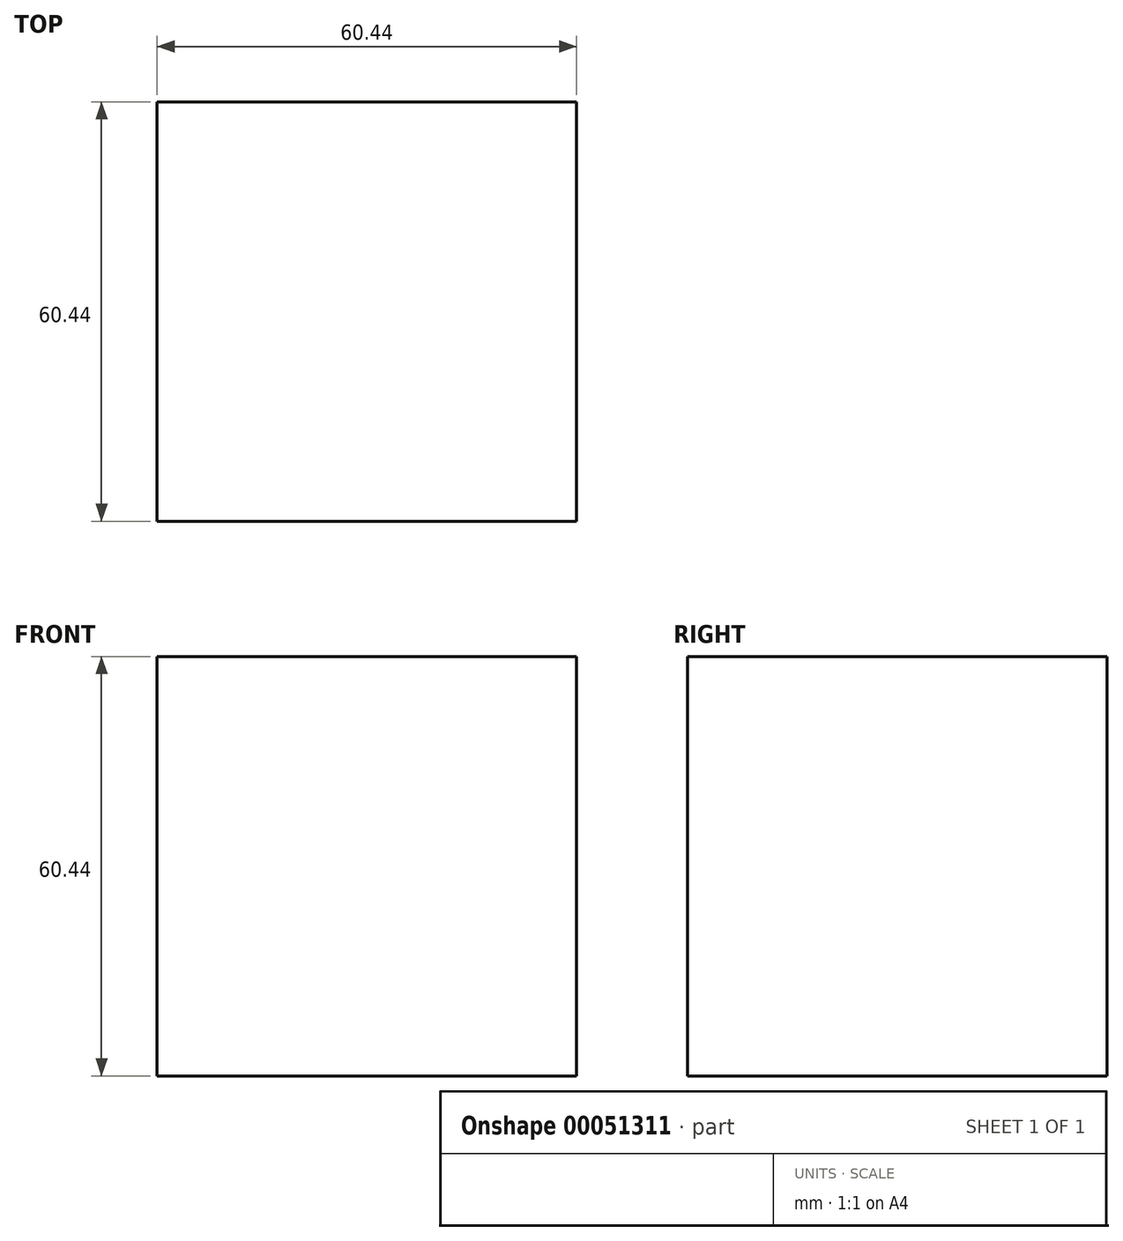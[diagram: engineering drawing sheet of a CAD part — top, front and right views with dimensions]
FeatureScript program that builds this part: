
annotation { "Feature Type Name" : "Feature", "Feature Type Description" : "" }
export const myFeature = defineFeature(function(context is Context, id is Id, definition is map)
    precondition{}
    {
        {
            var Q0;
            Q0=qCreatedBy(makeId("Top.planeOp"),FACE);
            var sketch = newSketch(context, id + "F0", { "sketchPlane" : qUnion([Q0])});
            skLineSegment(sketch, "E0.rect.bottom", {"start": v(-30.22, 30.22) * mm, "end": v(30.22, 30.22) * mm});
            skLineSegment(sketch, "E0.rect.top", {"start": v(-30.22, -30.22) * mm, "end": v(30.22, -30.22) * mm});
            skLineSegment(sketch, "E0.rect.left", {"start": v(-30.22, 30.22) * mm, "end": v(-30.22, -30.22) * mm});
            skLineSegment(sketch, "E0.rect.right", {"start": v(30.22, 30.22) * mm, "end": v(30.22, -30.22) * mm});
            skPoint(sketch, "E0.rect.middle", {"position": v(0, 0) * mm});
            skSolve(sketch);
        }
        {
            var Q0;
            Q0=qCreatedBy(makeId("Front.planeOp"),FACE);
            var sketch = newSketch(context, id + "F1", { "sketchPlane" : qUnion([Q0])});
            skLineSegment(sketch, "E1", {"start": v(0, 0) * mm, "end": v(0, 60.44) * mm});
            skSolve(sketch);
        }
        {
            var Q0;
            Q0=makeQuery(id+"F0.imprint","IMPRINT",FACE,{"disambiguationData":[TD([[makeQuery(id+"F0.imprint","IMPRINT",EDGE,{"derivedFrom":sQuery(id+"F0.wireOp",EDGE,"E0.rect.bottom")}),-1.0]])]});
            var Q1;
            Q1=sQuery(id+"F1.wireOp",EDGE,"E1");
            sweep(context, id + "F2", {"profiles" : qUnion([Q0]), "path" : qUnion([Q1])});
        }
    });
